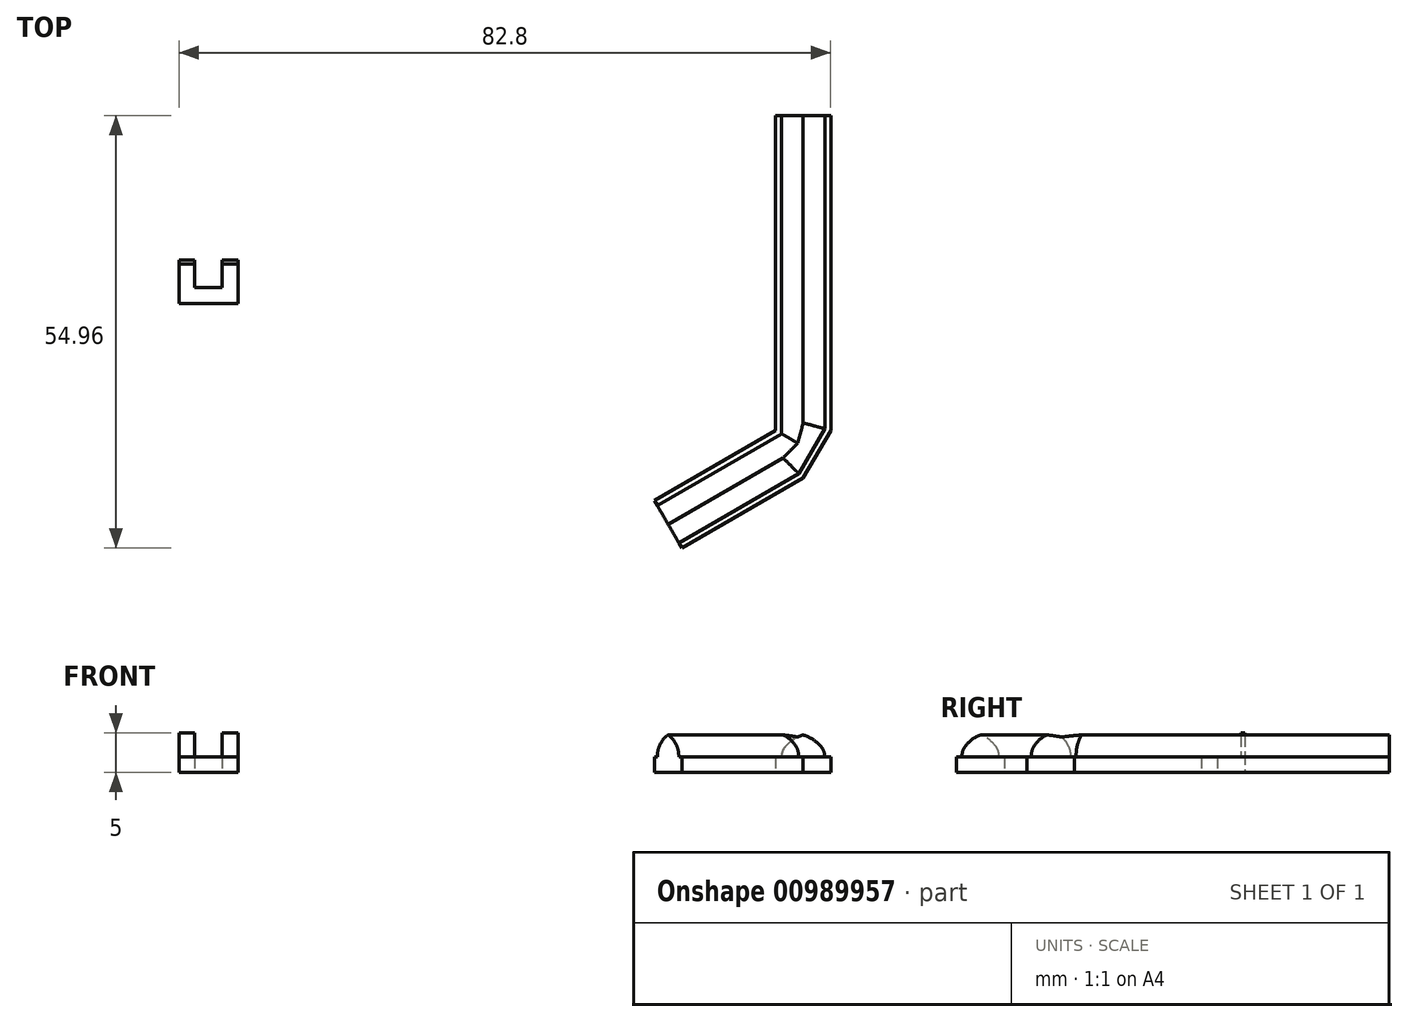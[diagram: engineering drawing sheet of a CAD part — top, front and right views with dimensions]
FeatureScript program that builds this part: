
annotation { "Feature Type Name" : "Feature", "Feature Type Description" : "" }
export const myFeature = defineFeature(function(context is Context, id is Id, definition is map)
    precondition{}
    {
        {
            var Q0;
            Q0=qCreatedBy(makeId("Top.planeOp"),FACE);
            var sketch = newSketch(context, id + "F0", { "sketchPlane" : qUnion([Q0])});
            skLineSegment(sketch, "E0", {"start": v(26.94, 29.28) * mm, "end": v(26.94, -10.72) * mm});
            skLineSegment(sketch, "E1", {"start": v(26.94, -10.72) * mm, "end": v(33.94, -10.72) * mm});
            skLineSegment(sketch, "E2", {"start": v(33.94, -10.72) * mm, "end": v(33.94, 29.28) * mm});
            skLineSegment(sketch, "E3", {"start": v(33.94, 29.28) * mm, "end": v(26.94, 29.28) * mm});
            skLineSegment(sketch, "E4", {"start": v(26.94, -10.72) * mm, "end": v(30.44, -16.78) * mm});
            skPoint(sketch, "E4.endSnap0", {"position": v(30.44, -10.72) * mm});
            skLineSegment(sketch, "E5", {"start": v(30.44, -16.78) * mm, "end": v(33.94, -10.72) * mm});
            skLineSegment(sketch, "E6", {"start": v(26.94, -10.72) * mm, "end": v(11.53, -19.62) * mm});
            skLineSegment(sketch, "E7", {"start": v(11.53, -19.62) * mm, "end": v(15.03, -25.68) * mm});
            skLineSegment(sketch, "E8", {"start": v(15.03, -25.68) * mm, "end": v(30.44, -16.78) * mm});
            skLineSegment(sketch, "E9", {"start": v(-48.86, 10.92) * mm, "end": v(-48.86, 5.42) * mm});
            skLineSegment(sketch, "E10", {"start": v(-48.86, 5.42) * mm, "end": v(-41.36, 5.42) * mm});
            skLineSegment(sketch, "E11", {"start": v(-41.36, 5.42) * mm, "end": v(-41.36, 10.92) * mm});
            skLineSegment(sketch, "E12", {"start": v(-46.86, 10.92) * mm, "end": v(-46.86, 7.42) * mm});
            skLineSegment(sketch, "E13", {"start": v(-46.86, 7.42) * mm, "end": v(-43.36, 7.42) * mm});
            skLineSegment(sketch, "E14", {"start": v(-43.36, 7.42) * mm, "end": v(-43.36, 10.92) * mm});
            skLineSegment(sketch, "E15", {"start": v(-46.86, 10.92) * mm, "end": v(-48.86, 10.92) * mm});
            skLineSegment(sketch, "E16", {"start": v(-43.36, 10.92) * mm, "end": v(-41.36, 10.92) * mm});
            skLineSegment(sketch, "E17", {"start": v(-48.86, 10.42) * mm, "end": v(-46.86, 10.42) * mm});
            skLineSegment(sketch, "E18", {"start": v(-43.36, 10.42) * mm, "end": v(-41.36, 10.42) * mm});
            skSolve(sketch);
        }
        {
            var Q0;
            Q0=makeQuery(id+"F0.imprint","IMPRINT",FACE,{"disambiguationData":[TD([[makeQuery(id+"F0.imprint","IMPRINT",EDGE,{"derivedFrom":sQuery(id+"F0.wireOp",EDGE,"E4")}),-1.0]])]});
            var Q1;
            Q1=makeQuery(id+"F0.imprint","IMPRINT",FACE,{"disambiguationData":[TD([[makeQuery(id+"F0.imprint","IMPRINT",EDGE,{"derivedFrom":sQuery(id+"F0.wireOp",EDGE,"E1")}),-1.0]])]});
            var Q2;
            Q2=makeQuery(id+"F0.imprint","IMPRINT",FACE,{"disambiguationData":[TD([[makeQuery(id+"F0.imprint","IMPRINT",EDGE,{"derivedFrom":sQuery(id+"F0.wireOp",EDGE,"E0")}),1.0]])]});
            extrude(context, id + "F1", {"entities" : qUnion([Q0, Q1, Q2]), "depth" : 5 * mm, "offsetDistance" : 25 * mm});
        }
        {
            var Q0;
            Q0=makeQuery(id+"F1.opExtrude","CAP_EDGE",EDGE,{"disambiguationData":[OSD([sQuery(id+"F0.wireOp",EDGE,"E0")])],"isStart":false});
            var Q1;
            Q1=makeQuery(id+"F1.opExtrude","CAP_EDGE",EDGE,{"disambiguationData":[OSD([sQuery(id+"F0.wireOp",EDGE,"E6")])],"isStart":false});
            var Q2;
            Q2=makeQuery(id+"F1.opExtrude","CAP_EDGE",EDGE,{"disambiguationData":[OSD([sQuery(id+"F0.wireOp",EDGE,"E5")])],"isStart":false});
            var Q3;
            Q3=makeQuery(id+"F1.opExtrude","CAP_EDGE",EDGE,{"disambiguationData":[OSD([sQuery(id+"F0.wireOp",EDGE,"E8")])],"isStart":false});
            var Q4;
            Q4=makeQuery(id+"F1.opExtrude","CAP_EDGE",EDGE,{"disambiguationData":[OSD([sQuery(id+"F0.wireOp",EDGE,"E2")])],"isStart":false});
            fillet(context, id + "F2", {"entities" : qUnion([Q0, Q1, Q2, Q3, Q4]), "radius" : 5 * mm, "tangentPropagation" : true, "allowEdgeOverflow" : false});
        }
        {
            var Q0;
            Q0=makeQuery(id+"F1.opExtrude","CAP_EDGE",EDGE,{"disambiguationData":[OSD([sQuery(id+"F0.wireOp",EDGE,"E7")])],"isStart":true});
            var Q1;
            {var subQ0=sQuery(id+"F0.wireOp",EDGE,"E8");Q1=makeQuery(id+"F2.opFillet","BLEND_EDGE",EDGE,{"blendedFrom":[makeQuery(id+"F1.opExtrude","CAP_EDGE",EDGE,{"disambiguationData":[OSD([subQ0])],"isStart":false}),makeQuery(id+"F1.opExtrude","CAP_FACE",FACE,{"disambiguationData":[OSD([sQuery(id+"F0.wireOp",EDGE,"E0"),sQuery(id+"F0.wireOp",EDGE,"E2"),sQuery(id+"F0.wireOp",EDGE,"E3"),sQuery(id+"F0.wireOp",EDGE,"E5"),sQuery(id+"F0.wireOp",EDGE,"E6"),sQuery(id+"F0.wireOp",EDGE,"E7"),subQ0])],"isStart":true})],"blendedInto":[makeQuery(id+"F1.opExtrude","CAP_FACE",FACE,{"disambiguationData":[OSD([sQuery(id+"F0.wireOp",EDGE,"E0"),sQuery(id+"F0.wireOp",EDGE,"E2"),sQuery(id+"F0.wireOp",EDGE,"E3"),sQuery(id+"F0.wireOp",EDGE,"E5"),sQuery(id+"F0.wireOp",EDGE,"E6"),sQuery(id+"F0.wireOp",EDGE,"E7"),subQ0])],"isStart":true})]});}
            var Q2;
            {var subQ0=sQuery(id+"F0.wireOp",EDGE,"E6");Q2=makeQuery(id+"F2.opFillet","BLEND_EDGE",EDGE,{"blendedFrom":[makeQuery(id+"F1.opExtrude","CAP_EDGE",EDGE,{"disambiguationData":[OSD([subQ0])],"isStart":false}),makeQuery(id+"F1.opExtrude","CAP_FACE",FACE,{"disambiguationData":[OSD([sQuery(id+"F0.wireOp",EDGE,"E0"),sQuery(id+"F0.wireOp",EDGE,"E2"),sQuery(id+"F0.wireOp",EDGE,"E3"),sQuery(id+"F0.wireOp",EDGE,"E5"),subQ0,sQuery(id+"F0.wireOp",EDGE,"E7"),sQuery(id+"F0.wireOp",EDGE,"E8")])],"isStart":true})],"blendedInto":[makeQuery(id+"F1.opExtrude","CAP_FACE",FACE,{"disambiguationData":[OSD([sQuery(id+"F0.wireOp",EDGE,"E0"),sQuery(id+"F0.wireOp",EDGE,"E2"),sQuery(id+"F0.wireOp",EDGE,"E3"),sQuery(id+"F0.wireOp",EDGE,"E5"),subQ0,sQuery(id+"F0.wireOp",EDGE,"E7"),sQuery(id+"F0.wireOp",EDGE,"E8")])],"isStart":true})]});}
            var Q3;
            {var subQ0=sQuery(id+"F0.wireOp",EDGE,"E0");Q3=makeQuery(id+"F2.opFillet","BLEND_EDGE",EDGE,{"blendedFrom":[makeQuery(id+"F1.opExtrude","CAP_EDGE",EDGE,{"disambiguationData":[OSD([subQ0])],"isStart":false}),makeQuery(id+"F1.opExtrude","CAP_FACE",FACE,{"disambiguationData":[OSD([subQ0,sQuery(id+"F0.wireOp",EDGE,"E2"),sQuery(id+"F0.wireOp",EDGE,"E3"),sQuery(id+"F0.wireOp",EDGE,"E5"),sQuery(id+"F0.wireOp",EDGE,"E6"),sQuery(id+"F0.wireOp",EDGE,"E7"),sQuery(id+"F0.wireOp",EDGE,"E8")])],"isStart":true})],"blendedInto":[makeQuery(id+"F1.opExtrude","CAP_FACE",FACE,{"disambiguationData":[OSD([subQ0,sQuery(id+"F0.wireOp",EDGE,"E2"),sQuery(id+"F0.wireOp",EDGE,"E3"),sQuery(id+"F0.wireOp",EDGE,"E5"),sQuery(id+"F0.wireOp",EDGE,"E6"),sQuery(id+"F0.wireOp",EDGE,"E7"),sQuery(id+"F0.wireOp",EDGE,"E8")])],"isStart":true})]});}
            var Q4;
            {var subQ0=sQuery(id+"F0.wireOp",EDGE,"E2");Q4=makeQuery(id+"F2.opFillet","BLEND_EDGE",EDGE,{"blendedFrom":[makeQuery(id+"F1.opExtrude","CAP_EDGE",EDGE,{"disambiguationData":[OSD([subQ0])],"isStart":false}),makeQuery(id+"F1.opExtrude","CAP_FACE",FACE,{"disambiguationData":[OSD([sQuery(id+"F0.wireOp",EDGE,"E0"),subQ0,sQuery(id+"F0.wireOp",EDGE,"E3"),sQuery(id+"F0.wireOp",EDGE,"E5"),sQuery(id+"F0.wireOp",EDGE,"E6"),sQuery(id+"F0.wireOp",EDGE,"E7"),sQuery(id+"F0.wireOp",EDGE,"E8")])],"isStart":true})],"blendedInto":[makeQuery(id+"F1.opExtrude","CAP_FACE",FACE,{"disambiguationData":[OSD([sQuery(id+"F0.wireOp",EDGE,"E0"),subQ0,sQuery(id+"F0.wireOp",EDGE,"E3"),sQuery(id+"F0.wireOp",EDGE,"E5"),sQuery(id+"F0.wireOp",EDGE,"E6"),sQuery(id+"F0.wireOp",EDGE,"E7"),sQuery(id+"F0.wireOp",EDGE,"E8")])],"isStart":true})]});}
            var Q5;
            {var subQ0=sQuery(id+"F0.wireOp",EDGE,"E5");Q5=makeQuery(id+"F2.opFillet","BLEND_EDGE",EDGE,{"blendedFrom":[makeQuery(id+"F1.opExtrude","CAP_EDGE",EDGE,{"disambiguationData":[OSD([subQ0])],"isStart":false}),makeQuery(id+"F1.opExtrude","CAP_FACE",FACE,{"disambiguationData":[OSD([sQuery(id+"F0.wireOp",EDGE,"E0"),sQuery(id+"F0.wireOp",EDGE,"E2"),sQuery(id+"F0.wireOp",EDGE,"E3"),subQ0,sQuery(id+"F0.wireOp",EDGE,"E6"),sQuery(id+"F0.wireOp",EDGE,"E7"),sQuery(id+"F0.wireOp",EDGE,"E8")])],"isStart":true})],"blendedInto":[makeQuery(id+"F1.opExtrude","CAP_FACE",FACE,{"disambiguationData":[OSD([sQuery(id+"F0.wireOp",EDGE,"E0"),sQuery(id+"F0.wireOp",EDGE,"E2"),sQuery(id+"F0.wireOp",EDGE,"E3"),subQ0,sQuery(id+"F0.wireOp",EDGE,"E6"),sQuery(id+"F0.wireOp",EDGE,"E7"),sQuery(id+"F0.wireOp",EDGE,"E8")])],"isStart":true})]});}
            var Q6;
            Q6=makeQuery(id+"F1.opExtrude","CAP_EDGE",EDGE,{"disambiguationData":[OSD([sQuery(id+"F0.wireOp",EDGE,"E3")])],"isStart":true});
            fillet(context, id + "F3", {"entities" : qUnion([Q0, Q1, Q2, Q3, Q4, Q5, Q6]), "radius" : 2 * mm, "tangentPropagation" : true, "allowEdgeOverflow" : false});
        }
        {
            var Q0;
            Q0=makeQuery(id+"F0.imprint","IMPRINT",FACE,{"disambiguationData":[TD([[makeQuery(id+"F0.imprint","IMPRINT",EDGE,{"derivedFrom":sQuery(id+"F0.wireOp",EDGE,"E0")}),1.0]])]});
            var Q1;
            Q1=makeQuery(id+"F0.imprint","IMPRINT",FACE,{"disambiguationData":[TD([[makeQuery(id+"F0.imprint","IMPRINT",EDGE,{"derivedFrom":sQuery(id+"F0.wireOp",EDGE,"E4")}),-1.0]])]});
            var Q2;
            Q2=makeQuery(id+"F0.imprint","IMPRINT",FACE,{"disambiguationData":[TD([[makeQuery(id+"F0.imprint","IMPRINT",EDGE,{"derivedFrom":sQuery(id+"F0.wireOp",EDGE,"E1")}),-1.0]])]});
            var Q3;
            {var subQ1=sQuery(id+"F0.wireOp",EDGE,"E10");Q3=makeQuery(id+"F0.imprint","IMPRINT",FACE,{"disambiguationData":[TD([[makeQuery(id+"F0.imprint","IMPRINT",EDGE,{"derivedFrom":subQ1}),1.0]])]});}
            extrude(context, id + "F4", {"entities" : qUnion([Q0, Q1, Q2, Q3]), "operationType" : NewBodyOperationType.ADD, "depth" : 2 * mm, "offsetDistance" : 25 * mm});
        }
        {
            var Q0;
            {var subQ0=sQuery(id+"F0.wireOp",EDGE,"E15");Q0=makeQuery(id+"F0.imprint","IMPRINT",FACE,{"disambiguationData":[TD([[makeQuery(id+"F0.imprint","IMPRINT",EDGE,{"derivedFrom":subQ0}),1.0]])]});}
            var Q1;
            {var subQ0=sQuery(id+"F0.wireOp",EDGE,"E16");Q1=makeQuery(id+"F0.imprint","IMPRINT",FACE,{"disambiguationData":[TD([[makeQuery(id+"F0.imprint","IMPRINT",EDGE,{"derivedFrom":subQ0}),-1.0]])]});}
            extrude(context, id + "F5", {"entities" : qUnion([Q0, Q1]), "operationType" : NewBodyOperationType.ADD, "depth" : 5 * mm, "offsetDistance" : 25 * mm});
        }
    });
